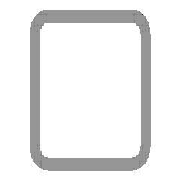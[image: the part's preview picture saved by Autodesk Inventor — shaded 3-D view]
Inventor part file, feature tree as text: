
AUTODESK INVENTOR PART (.ipt)
format: ipt  version: 2021 (Build 250183000, 183)  size: 130,048 bytes
history: native  units: mm (DEFAULTED — no unit token found)
features: other x4, sketch x3, extrude x1, plane x1
ambient origin geometry x8: Origin, YZ Plane, XZ Plane, XY Plane, X Axis, Y Axis, Z Axis, Center Point
bodies: Solid1 (feature_tree)
feature tree (9):
  parser-record x1  (decoder bookkeeping rows leaked as tree rows — omitted from the tree; the rows remain in map.json)
  other  "Driven Length"
  other  "Plano inicial"
  other  "Plano final"
  extrude  "Corpo"  TaperAngle=0.0deg  [1 undecoded]
  sketch  "Esboço"  dims[d11=50.8mm d12=4.7625mm d13=-0.0mm d14=1414.213562mm d15=25.4mm d16=25.4mm d17=9.525mm d18=90.0deg d19=1414.213562mm]
  sketch  "Sketch3"  dims[d3=1414.213562mm d4=0.0mm]
  plane  "Work Plane3"
  sketch  "Sketch4"  dims[d10=50.8mm]
note: 1 required parameter value undecoded (feature->parameter linkage not recoverable at this tier; creation-order binding heuristic only, values carry confidence <= 0.55)
